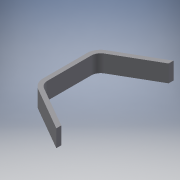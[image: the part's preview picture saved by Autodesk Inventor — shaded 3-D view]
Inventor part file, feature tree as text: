
AUTODESK INVENTOR PART (.ipt)
format: ipt  version: 2016 SP1 (Build 200210100, 210)  size: 107,520 bytes
history: native  units: mm
features: extrude x1, sketch x1
ambient origin geometry x8: Origin, YZ Plane, XZ Plane, XY Plane, X Axis, Y Axis, Z Axis, Center Point
bodies: Solid1 (feature_tree)
feature tree (2):
  extrude  "Extrusion1"  [1 undecoded]
  sketch  "Sketch1"  dims[d4=10.0mm d5=0.0mm]
note: 1 required parameter value undecoded (feature->parameter linkage not recoverable at this tier; creation-order binding heuristic only, values carry confidence <= 0.55)
